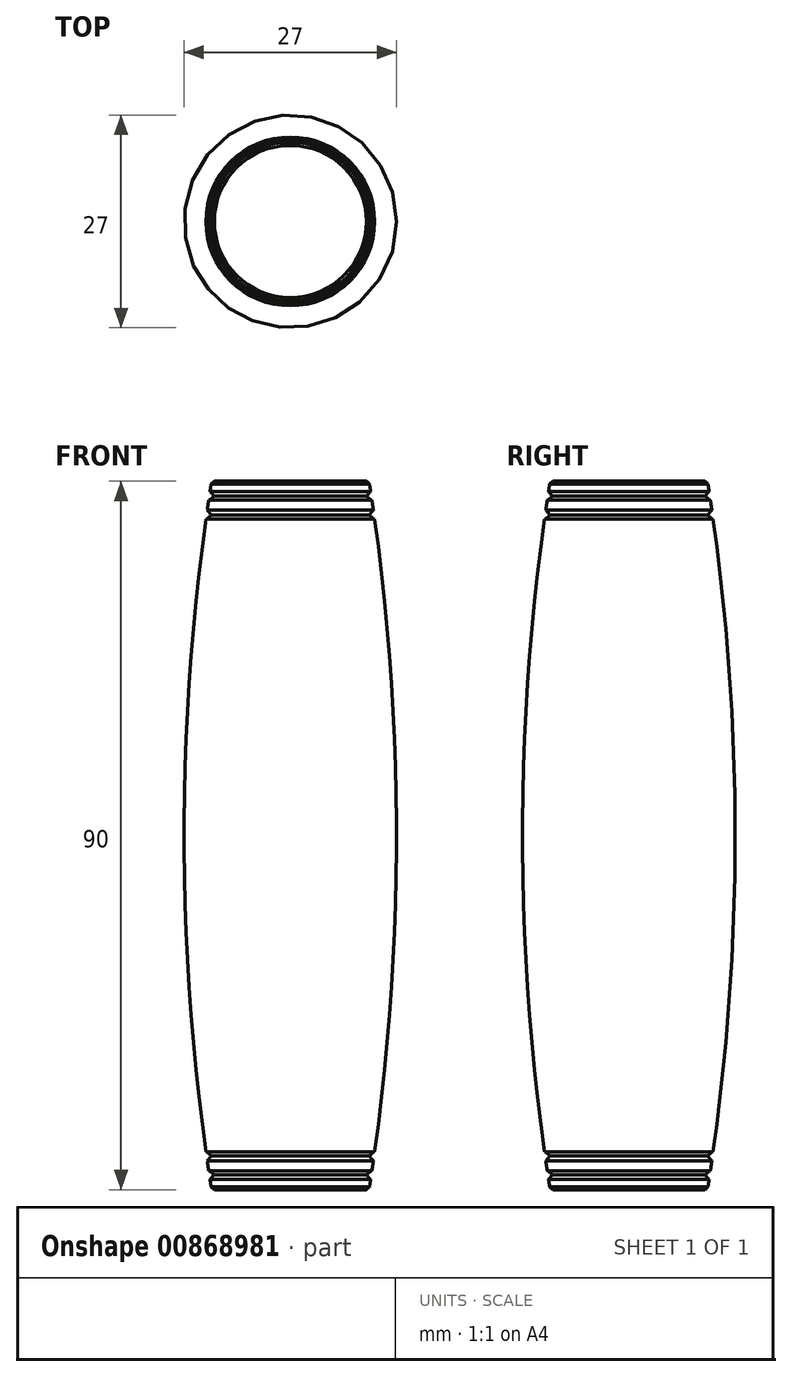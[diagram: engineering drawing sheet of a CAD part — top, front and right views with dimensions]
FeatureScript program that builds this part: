
annotation { "Feature Type Name" : "Feature", "Feature Type Description" : "" }
export const myFeature = defineFeature(function(context is Context, id is Id, definition is map)
    precondition{}
    {
        {
            var Q0;
            Q0=qCreatedBy(makeId("Front.planeOp"),FACE);
            var sketch = newSketch(context, id + "F0", { "sketchPlane" : qUnion([Q0])});
            skLineSegment(sketch, "E0", {"start": v(0, 45) * mm, "end": v(0, -45) * mm});
            skLineSegment(sketch, "E1", {"start": v(0, -45) * mm, "end": v(-10, -45) * mm});
            skLineSegment(sketch, "E2", {"start": v(0, 45) * mm, "end": v(-10, 45) * mm});
            skLineSegment(sketch, "E3", {"start": v(0, 0) * mm, "end": v(-13.5, 0) * mm, "construction": true});
            skArc(sketch, "E4", {"start": v(-10, 45) * mm, "mid": v(-13.5, 0) * mm, "end": v(-10, -45) * mm});
            skLineSegment(sketch, "E5", {"start": v(-10.19, 43.8) * mm, "end": v(-9.59, 43.8) * mm});
            skLineSegment(sketch, "E6", {"start": v(-9.59, 43.8) * mm, "end": v(-9.75, 42.6) * mm});
            skLineSegment(sketch, "E7", {"start": v(-9.75, 42.6) * mm, "end": v(-10.37, 42.6) * mm});
            skLineSegment(sketch, "E8", {"start": v(-10.54, 41.4) * mm, "end": v(-9.92, 41.4) * mm});
            skLineSegment(sketch, "E9", {"start": v(-9.92, 41.4) * mm, "end": v(-10.09, 40.2) * mm});
            skLineSegment(sketch, "E10", {"start": v(-10.09, 40.2) * mm, "end": v(-10.71, 40.2) * mm});
            skLineSegment(sketch, "E11", {"start": v(-9.75, 42.6) * mm, "end": v(-9.92, 41.4) * mm, "construction": true});
            skLineSegment(sketch, "E12.MirrorCS", {"start": v(-9.92, -41.4) * mm, "end": v(-10.09, -40.2) * mm});
            skLineSegment(sketch, "E13.MirrorCS", {"start": v(-9.59, -43.8) * mm, "end": v(-9.75, -42.6) * mm});
            skLineSegment(sketch, "E14.MirrorCS", {"start": v(-9.75, -42.6) * mm, "end": v(-10.37, -42.6) * mm});
            skLineSegment(sketch, "E15.MirrorCS", {"start": v(-10.09, -40.2) * mm, "end": v(-10.71, -40.2) * mm});
            skLineSegment(sketch, "E16.MirrorCS", {"start": v(-10.54, -41.4) * mm, "end": v(-9.92, -41.4) * mm});
            skLineSegment(sketch, "E17.MirrorCS", {"start": v(-9.75, -42.6) * mm, "end": v(-9.92, -41.4) * mm, "construction": true});
            skLineSegment(sketch, "E18.MirrorCS", {"start": v(-10.19, -43.8) * mm, "end": v(-9.59, -43.8) * mm});
            skSolve(sketch);
        }
        {
            var Q0;
            Q0=makeQuery(id+"F0.imprint","IMPRINT",FACE,{"disambiguationData":[TD([[makeQuery(id+"F0.imprint","IMPRINT",EDGE,{"derivedFrom":sQuery(id+"F0.wireOp",EDGE,"E0")}),-1.0]])]});
            var Q1;
            Q1=sQuery(id+"F0.wireOp",EDGE,"E0");
            revolve(context, id + "F1", {"surfaceOperationType" : NewSurfaceOperationType.NEW, "entities" : qUnion([Q0]), "axis" : qUnion([Q1]), "revolveType" : RevolveType.FULL});
        }
        {
            var Q0;
            Q0=makeQuery(id+"F1.opRevolve","SWEPT_FACE",FACE,{"disambiguationData":[OSD([sQuery(id+"F0.wireOp",EDGE,"E2")])]});
            var Q1;
            Q1=makeQuery(id+"F1.opRevolve","SWEPT_FACE",FACE,{"disambiguationData":[OSD([sQuery(id+"F0.wireOp",EDGE,"E1")])]});
            chamfer(context, id + "F2", {"entities" : qUnion([Q0, Q1]), "width" : .4 * mm, "tangentPropagation" : true});
        }
        {
            var Q0;
            Q0=makeQuery(id+"F1.opRevolve","SWEPT_FACE",FACE,{"disambiguationData":[OSD([sQuery(id+"F0.wireOp",EDGE,"E12.MirrorCS")])]});
            var Q1;
            Q1=makeQuery(id+"F1.opRevolve","SWEPT_FACE",FACE,{"disambiguationData":[OSD([sQuery(id+"F0.wireOp",EDGE,"E13.MirrorCS")])]});
            var Q2;
            Q2=makeQuery(id+"F1.opRevolve","SWEPT_FACE",FACE,{"disambiguationData":[OSD([sQuery(id+"F0.wireOp",EDGE,"E6")])]});
            var Q3;
            Q3=makeQuery(id+"F1.opRevolve","SWEPT_FACE",FACE,{"disambiguationData":[OSD([sQuery(id+"F0.wireOp",EDGE,"E9")])]});
            chamfer(context, id + "F3", {"entities" : qUnion([Q0, Q1, Q2, Q3]), "width" : .6 * mm, "tangentPropagation" : true});
        }
    });
